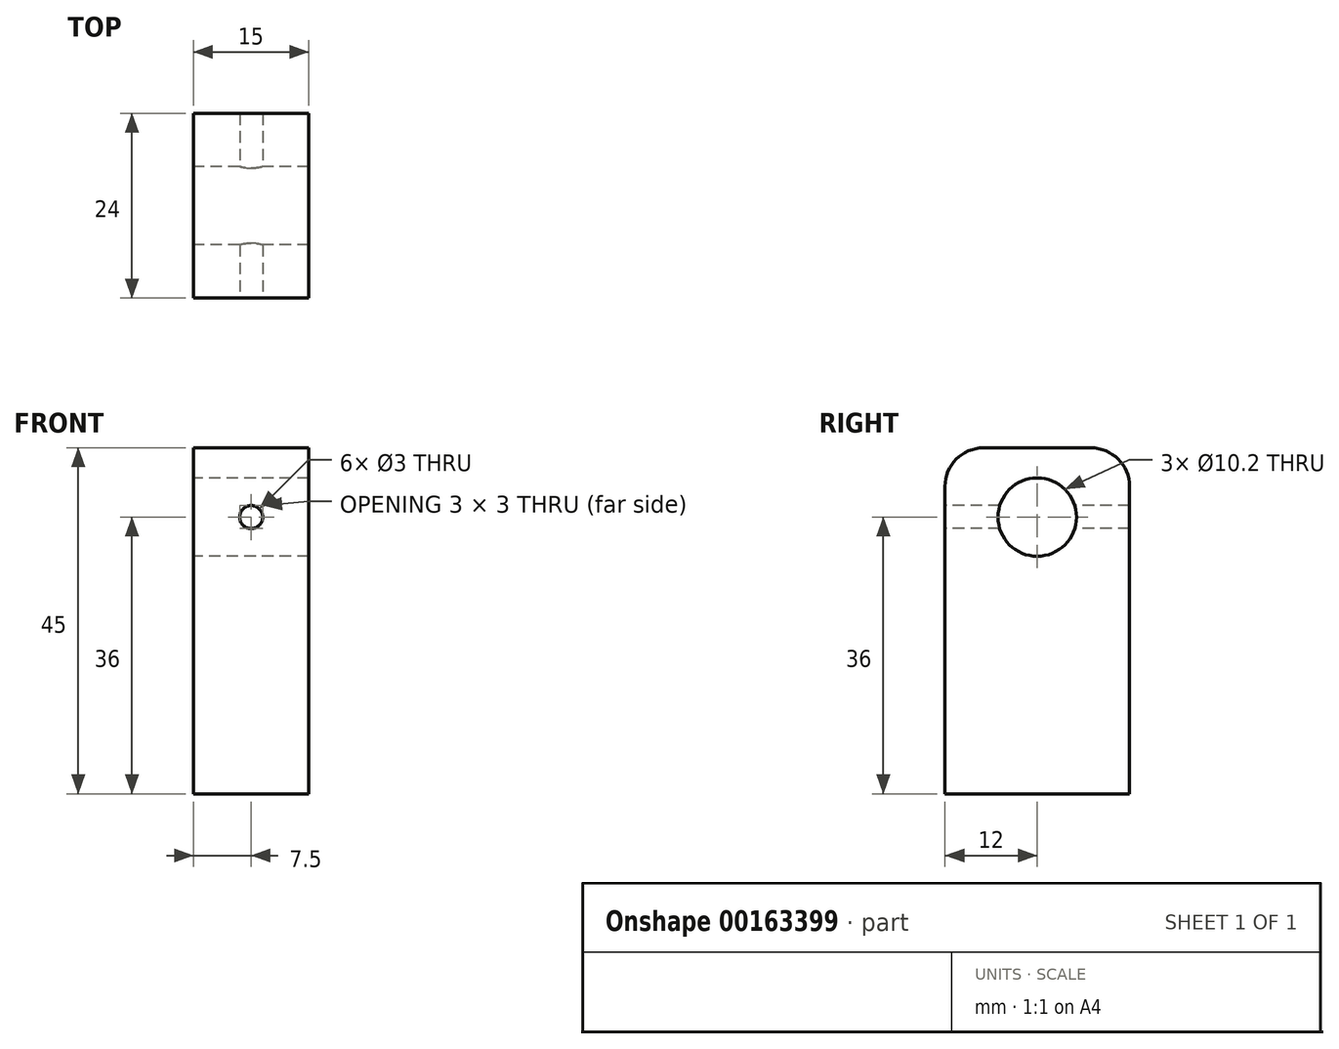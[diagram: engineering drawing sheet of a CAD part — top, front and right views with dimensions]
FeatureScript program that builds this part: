
annotation { "Feature Type Name" : "Feature", "Feature Type Description" : "" }
export const myFeature = defineFeature(function(context is Context, id is Id, definition is map)
    precondition{}
    {
        {
            var Q0;
            Q0=qCreatedBy(makeId("Right.planeOp"),FACE);
            var sketch = newSketch(context, id + "F0", { "sketchPlane" : qUnion([Q0])});
            skLineSegment(sketch, "E0.bottom", {"start": v(-12, 0) * mm, "end": v(12, 0) * mm});
            skLineSegment(sketch, "E0.top", {"start": v(-12, -45) * mm, "end": v(12, -45) * mm});
            skLineSegment(sketch, "E0.left", {"start": v(-12, 0) * mm, "end": v(-12, -45) * mm});
            skLineSegment(sketch, "E0.right", {"start": v(12, 0) * mm, "end": v(12, -45) * mm});
            skCircle(sketch, "E1", {"center": v(0, -9) * mm, "radius": 5.1 * mm});
            skSolve(sketch);
        }
        {
            var Q0;
            Q0=makeQuery(id+"F0.imprint","IMPRINT",FACE,{"disambiguationData":[TD([[makeQuery(id+"F0.imprint","IMPRINT",EDGE,{"derivedFrom":sQuery(id+"F0.wireOp",EDGE,"E0.bottom")}),-1.0]])]});
            extrude(context, id + "F1", {"entities" : qUnion([Q0]), "depth" : 15 * mm});
        }
        {
            var Q0;
            Q0=makeQuery(id+"F1.opExtrude","SWEPT_EDGE",EDGE,{"disambiguationData":[OSD([sQuery(id+"F0.wireOp",EDGE,"E0.bottom"),sQuery(id+"F0.wireOp",EDGE,"E0.right")])]});
            var Q1;
            Q1=makeQuery(id+"F1.opExtrude","SWEPT_EDGE",EDGE,{"disambiguationData":[OSD([sQuery(id+"F0.wireOp",EDGE,"E0.bottom"),sQuery(id+"F0.wireOp",EDGE,"E0.left")])]});
            fillet(context, id + "F2", {"entities" : qUnion([Q0, Q1]), "radius" : 5 * mm, "tangentPropagation" : true, "allowEdgeOverflow" : false});
        }
        {
            var Q0;
            Q0=makeQuery(id+"F1.opExtrude","SWEPT_FACE",FACE,{"disambiguationData":[OSD([sQuery(id+"F0.wireOp",EDGE,"E0.left")])]});
            var sketch = newSketch(context, id + "F3", { "sketchPlane" : qUnion([Q0])});
            skCircle(sketch, "E2", {"center": v(7.5, -9) * mm, "radius": 1.5 * mm});
            skSolve(sketch);
        }
        {
            var Q0;
            Q0=makeQuery(id+"F3.imprint","IMPRINT",FACE,{"disambiguationData":[TD([[makeQuery(id+"F3.imprint","IMPRINT",EDGE,{"derivedFrom":sQuery(id+"F3.wireOp",EDGE,"E2")}),1.0]])]});
            var Q1;
            Q1=sQuery(id+"F3.wireOp",EDGE,"E2");
            var Q2;
            Q2=makeQuery(id+"F1.opExtrude","SWEPT_FACE",FACE,{"disambiguationData":[OSD([sQuery(id+"F0.wireOp",EDGE,"E0.right")])]});
            extrude(context, id + "F4", {"entities" : qUnion([Q0]), "operationType" : NewBodyOperationType.REMOVE, "surfaceEntities" : qUnion([Q1]), "endBound" : BoundingType.UP_TO_SURFACE, "oppositeDirection" : true, "endBoundEntityFace" : qUnion([Q2]), "depth" : 25 * mm});
        }
    });
